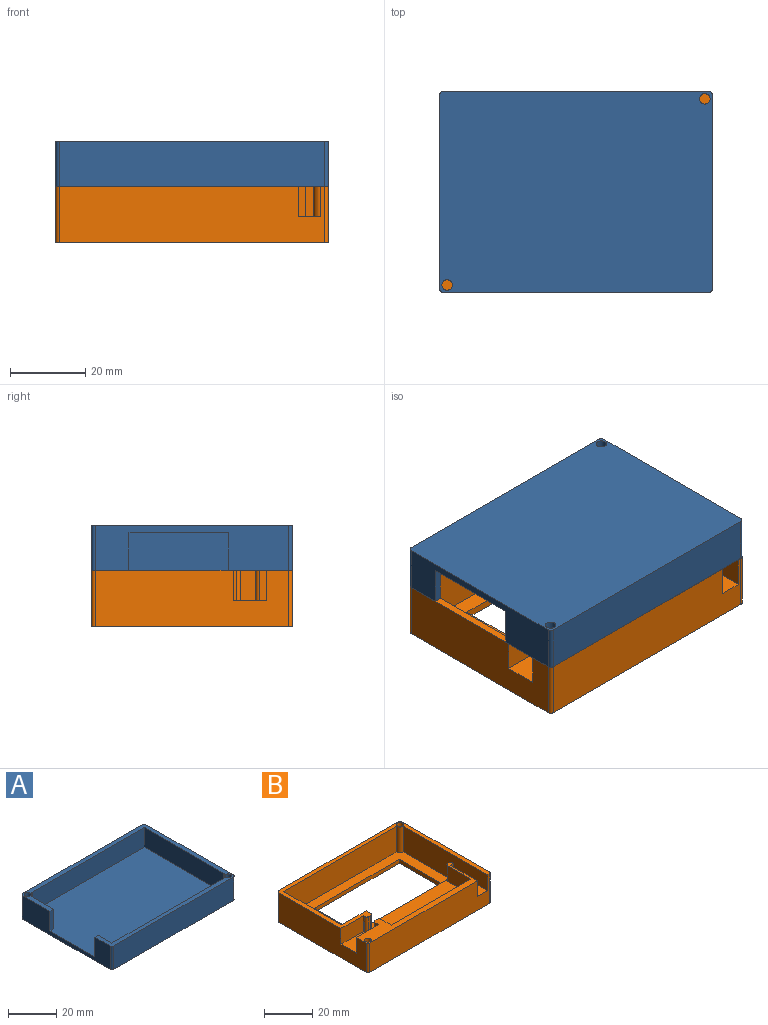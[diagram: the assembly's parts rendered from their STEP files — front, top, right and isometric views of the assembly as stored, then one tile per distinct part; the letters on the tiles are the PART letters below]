
ASSEMBLY  parts=2 mates=1
PART A: 22 faces, bbox 72.5x53.5x12 mm
  f0: plane 70.5x12mm, normal (0,1,0), area 846mm2, adj f15,f16,f18,f19
  f1: plane 10x2mm, normal (0,-1,0), area 20mm2, adj f2,f10,f15,f17
  f2: plane 13.1x10mm, normal (1,0,0), area 131mm2, adj f1,f3,f15,f17
  f3: cylinder r=1.9mm len=10mm, axis (0,0,-1), area 29.8mm2, adj f2,f4,f15,f17
  f4: plane 66.6x10mm, normal (0,-1,0), area 666mm2, adj f3,f5,f15,f17
  f5: plane 47.5x10mm, normal (-1,0,0), area 475mm2, adj f4,f6,f15,f17
  f6: cylinder r=2mm len=10mm, axis (0,0,-1), area 31.4mm2, adj f5,f7,f15,f17
  f7: plane 66.5x10mm, normal (0,1,0), area 665mm2, adj f6,f8,f15,f17
  f8: plane 10x8mm, normal (1,0,0), area 80mm2, adj f7,f9,f15,f17
  f9: plane 10x2mm, normal (0,1,0), area 20mm2, adj f8,f10,f15,f17
  f10: plane 51.5x12mm, normal (-1,0,0), area 353mm2, adj f1,f9,f15,f16,f17,f18,f21
  f11: plane 70.5x12mm, normal (0,-1,0), area 846mm2, adj f15,f16,f20,f21
  f12: cylinder r=1.4mm len=12mm, axis (0,0,-1), area 105.6mm2, adj f15,f16
  f13: plane 51.5x12mm, normal (1,0,0), area 618mm2, adj f15,f16,f19,f20
  f14: cylinder r=1.4mm len=12mm, axis (0,0,-1), area 105.6mm2, adj f15,f16
  f15: plane 72.5x53.5mm, normal (0,0,1), area 427.8mm2, adj f0,f1,f2,f3,f4,f5,f6,f7
  f16: plane 72.5x53.5mm, normal (0,0,-1), area 3865.6mm2, adj f0,f10,f11,f12,f13,f14,f18,f19
  f17: plane 70.5x49.5mm, normal (0,0,1), area 3437.8mm2, adj f1,f2,f3,f4,f5,f6,f7,f8
  f18: cylinder r=1mm len=12mm, axis (0,0,-1), area 18.8mm2, adj f0,f10,f15,f16
  f19: cylinder r=1mm len=12mm, axis (0,0,-1), area 18.8mm2, adj f0,f13,f15,f16
  f20: cylinder r=1mm len=12mm, axis (0,0,-1), area 18.8mm2, adj f11,f13,f15,f16
  f21: cylinder r=1mm len=12mm, axis (0,0,-1), area 18.8mm2, adj f10,f11,f15,f16
PART B: 46 faces, bbox 72.5x53.5x15 mm
  f0: plane 64.5x14.67mm, normal (0,0,1), area 821.7mm2, adj f9,f15,f23,f24,f25,f26,f27,f28
  f1: cylinder r=1.9mm len=13mm, axis (0,0,-1), area 38.8mm2, adj f3,f10,f11,f18
  f2: plane 17.5x6mm, normal (0,0,1), area 101.9mm2, adj f9,f10,f12,f20,f21,f22,f40
  f3: plane 68.5x34mm, normal (0,0,1), area 1026.2mm2, adj f1,f4,f5,f6,f7,f9,f10,f11
  f4: plane 26x2mm, normal (1,0,0), area 52mm2, adj f3,f5,f7,f8
  f5: plane 50x2mm, normal (0,-1,0), area 100mm2, adj f3,f4,f6,f8
  f6: plane 26x2mm, normal (-1,0,0), area 52mm2, adj f3,f5,f7,f8
  f7: plane 50x2mm, normal (0,1,0), area 100mm2, adj f3,f4,f6,f8
  f8: plane 72.5x53.5mm, normal (0,0,-1), area 2577.9mm2, adj f4,f5,f6,f7,f12,f13,f14,f15
  f9: plane 68.5x13mm, normal (0,1,0), area 466.5mm2, adj f0,f2,f3,f10,f16,f18,f29,f33
  f10: plane 49.6x13mm, normal (-1,0,0), area 557.3mm2, adj f1,f2,f3,f9,f12,f18
  f11: plane 66.6x13mm, normal (0,-1,0), area 865.8mm2, adj f1,f3,f16,f18
  f12: plane 70.5x15mm, normal (0,-1,0), area 1009.5mm2, adj f2,f8,f10,f18,f20,f29,f42,f43
  f13: plane 51.5x15mm, normal (1,0,0), area 772.5mm2, adj f8,f18,f43,f44
  f14: plane 70.5x15mm, normal (0,1,0), area 1057.5mm2, adj f8,f18,f44,f45
  f15: plane 51.5x15mm, normal (-1,0,0), area 700.5mm2, adj f0,f8,f18,f28,f29,f30,f42,f45
  f16: plane 34x13mm, normal (1,0,0), area 442mm2, adj f3,f9,f11,f18
  f17: cylinder r=1.4mm len=13mm, axis (0,0,-1), area 114.4mm2, adj f18,f19
  f18: plane 72.5x53.5mm, normal (0,0,1), area 346.2mm2, adj f1,f9,f10,f11,f12,f13,f14,f15
  f19: plane 2.8x2.8mm, normal (0,0,1), area 6.2mm2, adj f17
  f20: plane 15.83x8mm, normal (1,0,0), area 126.6mm2, adj f2,f12,f21,f29
  f21: plane 8x2mm, normal (0,-1,0), area 16mm2, adj f2,f20,f22,f29
  f22: plane 8x0.67mm, normal (1,0,0), area 5.4mm2, adj f2,f21,f29,f40
  f23: plane 13.67x8mm, normal (-1,0,0), area 109.4mm2, adj f0,f24,f29,f41
  f24: plane 47x8mm, normal (0,1,0), area 376mm2, adj f0,f23,f25,f29
  f25: plane 8x6mm, normal (1,0,0), area 48mm2, adj f0,f24,f29,f38
  f26: plane 8x1.5mm, normal (0,1,0), area 12mm2, adj f0,f29,f38,f39
  f27: plane 8x2mm, normal (-1,0,0), area 16mm2, adj f0,f28,f29,f39
  f28: plane 13x8mm, normal (0,1,0), area 104mm2, adj f0,f15,f27,f29
  f29: plane 66.5x17.5mm, normal (0,0,1), area 269.7mm2, adj f9,f12,f15,f20,f21,f22,f23,f24
  f30: plane 13x8mm, normal (0,-1,0), area 104mm2, adj f0,f15,f18,f31
  f31: plane 8x1mm, normal (-1,0,0), area 8mm2, adj f0,f18,f30,f36
  f32: plane 8x1.5mm, normal (0,-1,0), area 12mm2, adj f0,f18,f36,f37
  f33: plane 8x2.67mm, normal (1,0,0), area 21.4mm2, adj f0,f9,f18,f37
  f34: plane 2.8x2.8mm, normal (0,0,1), area 6.2mm2, adj f35
  f35: cylinder r=1.4mm len=13mm, axis (0,0,-1), area 114.4mm2, adj f29,f34
  f36: cylinder r=1mm len=8mm, axis (0,0,-1), area 12.6mm2, adj f0,f18,f31,f32
  f37: cylinder r=1mm len=8mm, axis (0,0,-1), area 12.6mm2, adj f0,f18,f32,f33
  f38: cylinder r=1mm len=8mm, axis (0,0,1), area 12.6mm2, adj f0,f25,f26,f29
  f39: cylinder r=1mm len=8mm, axis (0,0,-1), area 12.6mm2, adj f0,f26,f27,f29
  f40: cylinder r=1mm len=8mm, axis (0,0,1), area 12.6mm2, adj f2,f9,f22,f29
  f41: cylinder r=1mm len=8mm, axis (0,0,-1), area 12.6mm2, adj f0,f9,f23,f29
  f42: cylinder r=1mm len=15mm, axis (0,0,-1), area 23.6mm2, adj f8,f12,f15,f29
  f43: cylinder r=1mm len=15mm, axis (0,0,-1), area 23.6mm2, adj f8,f12,f13,f18
  f44: cylinder r=1mm len=15mm, axis (0,0,-1), area 23.6mm2, adj f8,f13,f14,f18
  f45: cylinder r=1mm len=15mm, axis (0,0,-1), area 23.6mm2, adj f8,f14,f15,f18
PLACE A rot(axis=(1,0,0),180deg) t=(28.11,-87.01,-14.98)mm
PLACE B t=(32.58,-61.88,-41.98)mm
MATE fastened A.f13 <-> B.f13  axis (1,0,0) through (64.36,-74.45,-26.98)mm
